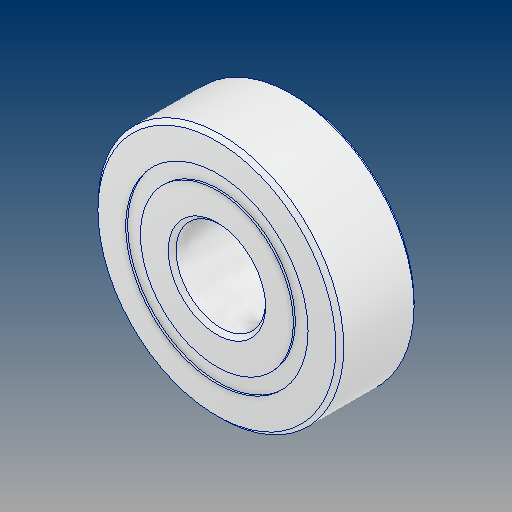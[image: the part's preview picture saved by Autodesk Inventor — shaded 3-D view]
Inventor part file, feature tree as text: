
AUTODESK INVENTOR PART (.ipt)
format: ipt  version: 2020 (Build 240168000, 168)  size: 227,328 bytes
history: native  units: in
note: dims shown in document units (in); Inventor stores cm internally (conversion verified against a paired STEP export)
features: revolve x4
ambient origin geometry x8: Origin, YZ Plane, XZ Plane, XY Plane, X Axis, Y Axis, Z Axis, Center Point
bodies: Solid1 (feature_tree), Solid2 (feature_tree), Solid15 (feature_tree), Solid16 (feature_tree)
feature tree (4):
  revolve  "Revolve1"  [1 undecoded]
  revolve  "Revolve3"  [1 undecoded]
  revolve  "Revolve5[1]"  [1 undecoded]
  revolve  "Revolve5[2]"  [1 undecoded]
note: 4 required parameter values undecoded (feature->parameter linkage not recoverable at this tier; creation-order binding heuristic only, values carry confidence <= 0.55)
